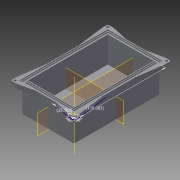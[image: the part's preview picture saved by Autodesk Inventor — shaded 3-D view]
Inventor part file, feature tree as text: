
AUTODESK INVENTOR PART (.ipt)
format: ipt  version: 2015 SP2 (Build 190223200, 223)  size: 287,744 bytes
history: native  units: in
note: dims shown in document units (in); Inventor stores cm internally (conversion verified against a paired STEP export)
features: sketch x8, extrude x7, projected_geometry x7, plane x3, hole x2, fillet x2, mirror x2, other x1
ambient origin geometry x8: Origin, YZ Plane, XZ Plane, XY Plane, X Axis, Y Axis, Z Axis, Center Point
bodies: Solid1 (feature_tree)
feature tree (32):
  extrude  "Extrusion1"  Depth=4.6489in
  extrude  "Extrusion2"  Depth=0.0394in
  extrude  "Extrusion3"  Depth=0.0394in
  extrude  "Extrusion4"  Depth=0.0394in
  extrude  "Extrusion6"  Depth=0.0394in TaperAngle=0.0deg
  extrude  "Extrusion5"  Depth=0.0394in
  hole  "Hole1"  [1 undecoded]
  fillet  "Fillet1"  Radius=0.315in
  extrude  "Extrusion7"  Depth=0.2362in
  fillet  "Fillet2"  Radius=4.6489in
  sketch  "Sketch12"  dims[d19=0.0787in d20=0.0in d21=0.2362in d22=0.1181in d23=0.2362in d24=0.1575in d25=0.0787in d26=90.0deg d27=0.315in d28=0.8108in d29=4.6489in d30=0.0787in d31=0.1181in d32=0.0394in d33=0.1181in d34=0.2362in d35=0.1181in d36=0.1181in d37=45.0deg d47=1.0532in d50=0.0394in d51=0.0394in d52=0.1181in d53=0.0394in d54=0.0in d55=0.0in d56=0.2362in d57=0.2362in d58=0.1575in d59=0.0in d60=0.0787in d61=0.1181in d62=0.1181in d63=0.2362in d64=0.1575in d65=0.0787in d66=90.0deg d67=0.315in d68=0.8108in d69=2.4937in d70=4.334in]
  other  "Work Point1"
  hole  "Hole2"  [1 undecoded]
  plane  "Work Plane1"
  plane  "Work Plane5"
  plane  "Work Plane6"
  mirror  "Mirror6"
  mirror  "Mirror7"
  sketch  "Sketch1"  dims[d0=2.8087in d1=4.6489in]
  sketch  "Sketch2"  dims[d2=0.0394in d3=0.0in d4=0.0394in]
  projected_geometry  "Projected Loop1"
  sketch  "Sketch3"  dims[d5=1.378in d6=0.0in d7=0.0394in]
  projected_geometry  "Projected Loop2"
  sketch  "Sketch4"  dims[d8=0.0394in d9=0.0394in]
  projected_geometry  "Projected Loop3"
  sketch  "Sketch5"  dims[d10=0.0394in d11=0.0394in d12=0.0in]
  projected_geometry  "Projected Loop4"
  sketch  "Sketch10"  dims[d13=0.0394in d14=0.0394in]
  projected_geometry  "Projected Loop5"
  projected_geometry  "Projected Loop6"
  projected_geometry  "Projected Loop7"
  sketch  "Sketch11"  dims[d15=0.0591in d16=0.0in d17=0.315in d18=0.315in]
note: 2 required parameter values undecoded (feature->parameter linkage not recoverable at this tier; creation-order binding heuristic only, values carry confidence <= 0.55)
